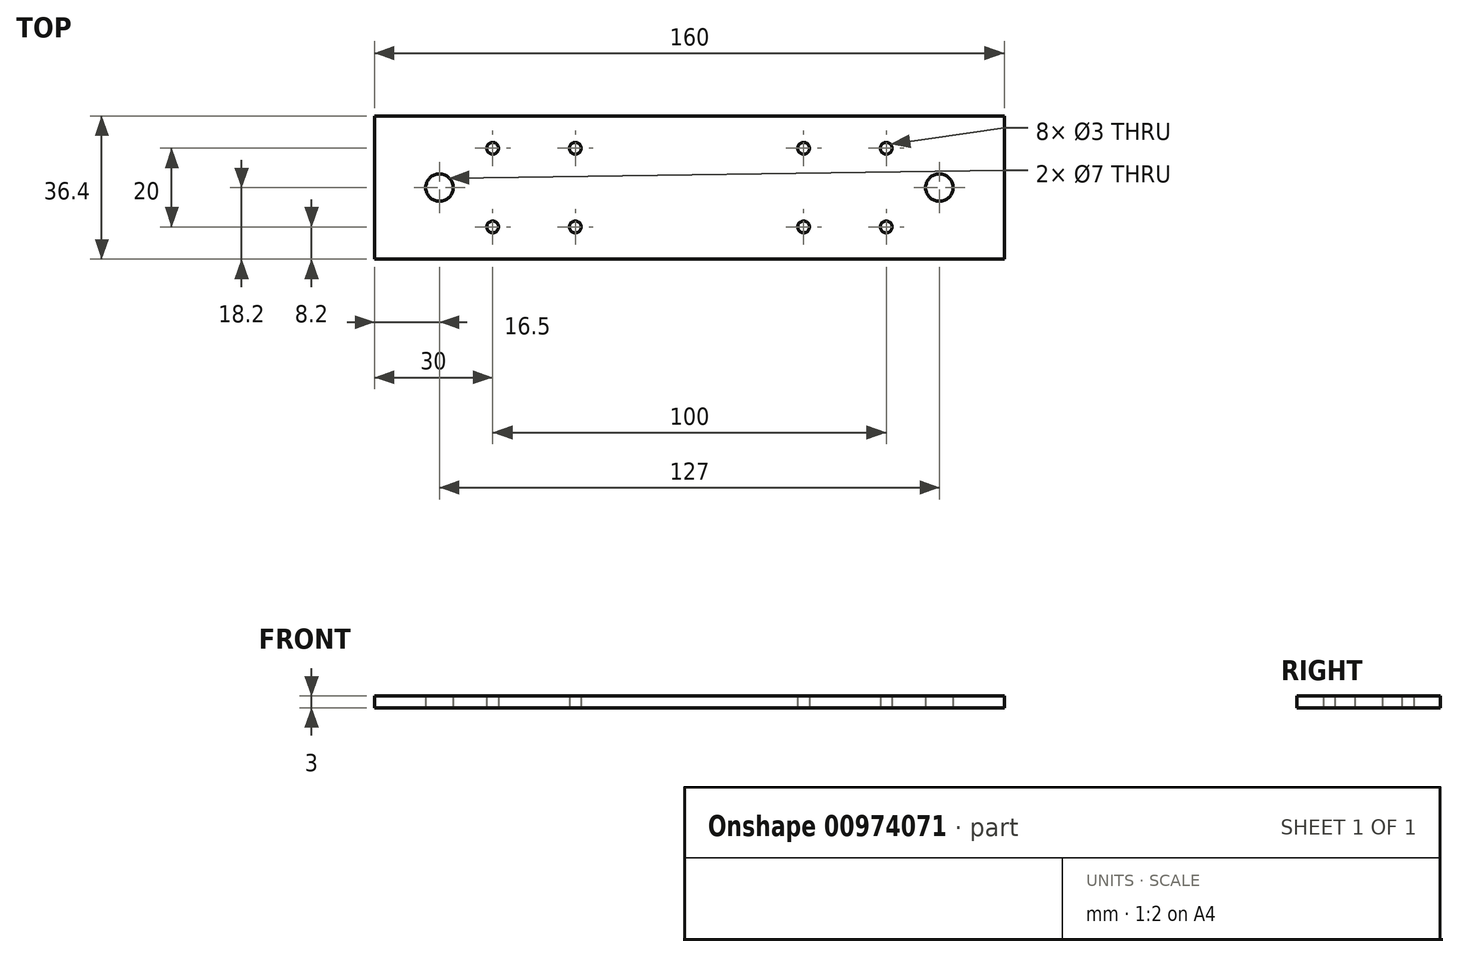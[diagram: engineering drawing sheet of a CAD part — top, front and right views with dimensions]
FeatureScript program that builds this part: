
annotation { "Feature Type Name" : "Feature", "Feature Type Description" : "" }
export const myFeature = defineFeature(function(context is Context, id is Id, definition is map)
    precondition{}
    {
        {
            var Q0;
            Q0=qCreatedBy(makeId("Top.planeOp"),FACE);
            var sketch = newSketch(context, id + "F0", { "sketchPlane" : qUnion([Q0])});
            skLineSegment(sketch, "E0.bottom", {"start": v(80, -18.2) * mm, "end": v(-80, -18.2) * mm});
            skLineSegment(sketch, "E0.top", {"start": v(80, 18.2) * mm, "end": v(-80, 18.2) * mm});
            skLineSegment(sketch, "E0.left", {"start": v(80, -18.2) * mm, "end": v(80, 18.2) * mm});
            skLineSegment(sketch, "E0.right", {"start": v(-80, -18.2) * mm, "end": v(-80, 18.2) * mm});
            skPoint(sketch, "E0.middle", {"position": v(0, 0) * mm});
            skLineSegment(sketch, "E1", {"start": v(0, 60.36) * mm, "end": v(0, -47.58) * mm, "construction": true});
            skLineSegment(sketch, "E2", {"start": v(-105.47, 0) * mm, "end": v(118.72, 0) * mm, "construction": true});
            skCircle(sketch, "E3", {"center": v(-63.5, 0) * mm, "radius": 3.5 * mm});
            skCircle(sketch, "E4", {"center": v(-50, 10) * mm, "radius": 1.5 * mm});
            skCircle(sketch, "E5", {"center": v(-50, -10) * mm, "radius": 1.5 * mm});
            skCircle(sketch, "E6.MirrorC", {"center": v(50, 10) * mm, "radius": 1.5 * mm});
            skCircle(sketch, "E7.MirrorC", {"center": v(63.5, 0) * mm, "radius": 3.5 * mm});
            skCircle(sketch, "E8.MirrorC", {"center": v(50, -10) * mm, "radius": 1.5 * mm});
            skCircle(sketch, "E9", {"center": v(-29, 10) * mm, "radius": 1.5 * mm});
            skCircle(sketch, "E10", {"center": v(-29, -10) * mm, "radius": 1.5 * mm});
            skCircle(sketch, "E11.MirrorC", {"center": v(29, 10) * mm, "radius": 1.5 * mm});
            skCircle(sketch, "E12.MirrorC", {"center": v(29, -10) * mm, "radius": 1.5 * mm});
            skSolve(sketch);
        }
        {
            var Q0;
            Q0=makeQuery(id+"F0.imprint","IMPRINT",FACE,{"disambiguationData":[TD([[makeQuery(id+"F0.imprint","IMPRINT",EDGE,{"derivedFrom":sQuery(id+"F0.wireOp",EDGE,"E0.bottom")}),-1.0]])]});
            extrude(context, id + "F1", {"entities" : qUnion([Q0]), "depth" : 3 * mm, "offsetDistance" : 25 * mm});
        }
    });
